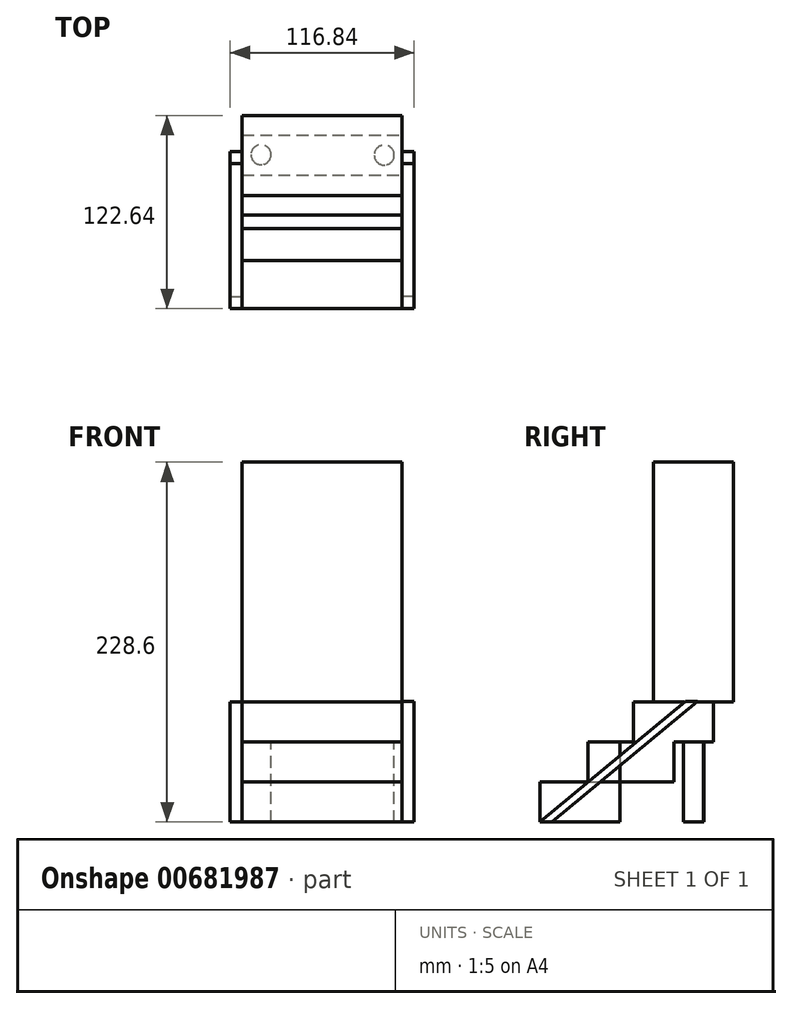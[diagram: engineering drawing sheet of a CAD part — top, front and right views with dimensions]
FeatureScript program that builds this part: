
annotation { "Feature Type Name" : "Feature", "Feature Type Description" : "" }
export const myFeature = defineFeature(function(context is Context, id is Id, definition is map)
    precondition{}
    {
        {
            var Q0;
            Q0=qCreatedBy(makeId("Top.planeOp"),FACE);
            var sketch = newSketch(context, id + "F0", { "sketchPlane" : qUnion([Q0])});
            skLineSegment(sketch, "E0.bottom", {"start": v(-36.45, 27.56) * mm, "end": v(65.15, 27.56) * mm});
            skLineSegment(sketch, "E0.top", {"start": v(-36.45, -23.24) * mm, "end": v(65.15, -23.24) * mm});
            skLineSegment(sketch, "E0.left", {"start": v(-36.45, 27.56) * mm, "end": v(-36.45, -23.24) * mm});
            skLineSegment(sketch, "E0.right", {"start": v(65.15, 27.56) * mm, "end": v(65.15, -23.24) * mm});
            skSolve(sketch);
        }
        {
            var Q0;
            Q0=makeQuery(id+"F0.imprint","IMPRINT",FACE,{"disambiguationData":[TD([[makeQuery(id+"F0.imprint","IMPRINT",EDGE,{"derivedFrom":sQuery(id+"F0.wireOp",EDGE,"E0.bottom")}),-1.0]])]});
            extrude(context, id + "F1", {"entities" : qUnion([Q0]), "depth" : 25.4 * mm, "offsetDistance" : 25.4 * mm});
        }
        {
            var Q0;
            Q0=makeQuery(id+"F1.opExtrude","CAP_FACE",FACE,{"disambiguationData":[OSD([sQuery(id+"F0.wireOp",EDGE,"E0.bottom"),sQuery(id+"F0.wireOp",EDGE,"E0.top"),sQuery(id+"F0.wireOp",EDGE,"E0.left"),sQuery(id+"F0.wireOp",EDGE,"E0.right")])],"isStart":false});
            var sketch = newSketch(context, id + "F2", { "sketchPlane" : qUnion([Q0])});
            skLineSegment(sketch, "E1.bottom", {"start": v(-36.45, 10.8) * mm, "end": v(65.15, 10.8) * mm});
            skLineSegment(sketch, "E1.top", {"start": v(-36.45, 61.6) * mm, "end": v(65.15, 61.6) * mm});
            skLineSegment(sketch, "E1.left", {"start": v(-36.45, 10.8) * mm, "end": v(-36.45, 61.6) * mm});
            skLineSegment(sketch, "E1.right", {"start": v(65.15, 10.8) * mm, "end": v(65.15, 61.6) * mm});
            skSolve(sketch);
        }
        {
            var Q0;
            {var subQ3=sQuery(id+"F2.wireOp",EDGE,"E1.top");Q0=makeQuery(id+"F2.imprint","IMPRINT",FACE,{"disambiguationData":[TD([[makeQuery(id+"F2.imprint","IMPRINT",EDGE,{"derivedFrom":subQ3}),-1.0]])]});}
            extrude(context, id + "F3", {"entities" : qUnion([Q0]), "depth" : 25.4 * mm, "offsetDistance" : 25.4 * mm});
        }
        {
            var Q0;
            Q0=makeQuery(id+"F3.opExtrude","SWEPT_FACE",FACE,{"disambiguationData":[OSD([sQuery(id+"F0.wireOp",EDGE,"E0.bottom")])]});
            extrude(context, id + "F4", {"entities" : qUnion([Q0]), "depth" : 20.32 * mm, "offsetDistance" : 25.4 * mm});
        }
        {
            var Q0;
            Q0=makeQuery(id+"F3.opExtrude","CAP_FACE",FACE,{"disambiguationData":[OSD([sQuery(id+"F0.wireOp",EDGE,"E0.bottom"),sQuery(id+"F0.wireOp",EDGE,"E0.right"),sQuery(id+"F2.wireOp",EDGE,"E1.bottom"),sQuery(id+"F2.wireOp",EDGE,"E1.top"),sQuery(id+"F2.wireOp",EDGE,"E1.left"),sQuery(id+"F2.wireOp",EDGE,"E1.right")])],"isStart":false});
            var sketch = newSketch(context, id + "F5", { "sketchPlane" : qUnion([Q0])});
            skLineSegment(sketch, "E2.bottom", {"start": v(-36.45, 36.13) * mm, "end": v(65.15, 36.13) * mm});
            skLineSegment(sketch, "E2.top", {"start": v(-36.45, 86.93) * mm, "end": v(65.15, 86.93) * mm});
            skLineSegment(sketch, "E2.left", {"start": v(-36.45, 36.13) * mm, "end": v(-36.45, 86.93) * mm});
            skLineSegment(sketch, "E2.right", {"start": v(65.15, 36.13) * mm, "end": v(65.15, 86.93) * mm});
            skSolve(sketch);
        }
        {
            var Q0;
            {var subQ0=sQuery(id+"F5.wireOp",EDGE,"E2.top");Q0=makeQuery(id+"F5.imprint","IMPRINT",FACE,{"disambiguationData":[TD([[makeQuery(id+"F5.imprint","IMPRINT",EDGE,{"derivedFrom":subQ0}),-1.0]])]});}
            var Q1;
            {var subQ0=sQuery(id+"F5.wireOp",EDGE,"E2.bottom");Q1=makeQuery(id+"F5.imprint","IMPRINT",FACE,{"disambiguationData":[TD([[makeQuery(id+"F5.imprint","IMPRINT",EDGE,{"derivedFrom":subQ0}),1.0]])]});}
            extrude(context, id + "F6", {"entities" : qUnion([Q0, Q1]), "operationType" : NewBodyOperationType.ADD, "depth" : 25.4 * mm, "offsetDistance" : 25.4 * mm});
        }
        {
            var Q0;
            Q0=makeQuery(id+"F6.opExtrude","CAP_FACE",FACE,{"disambiguationData":[OSD([sQuery(id+"F5.wireOp",EDGE,"E2.bottom"),sQuery(id+"F5.wireOp",EDGE,"E2.top"),sQuery(id+"F5.wireOp",EDGE,"E2.left"),sQuery(id+"F5.wireOp",EDGE,"E2.right")])],"isStart":true});
            var sketch = newSketch(context, id + "F7", { "sketchPlane" : qUnion([Q0])});
            skCircle(sketch, "E3", {"center": v(-24.5, -74.53) * mm, "radius": 6.35 * mm});
            skCircle(sketch, "E4", {"center": v(53.76, -74.26) * mm, "radius": 6.35 * mm});
            skPoint(sketch, "E4.centerSnap0", {"position": v(-36.45, -74.26) * mm});
            skSolve(sketch);
        }
        {
            var Q0;
            Q0=makeQuery(id+"F7.imprint","IMPRINT",FACE,{"disambiguationData":[TD([[makeQuery(id+"F7.imprint","IMPRINT",EDGE,{"derivedFrom":sQuery(id+"F7.wireOp",EDGE,"E3")}),1.0]])]});
            var Q1;
            Q1=makeQuery(id+"F7.imprint","IMPRINT",FACE,{"disambiguationData":[TD([[makeQuery(id+"F7.imprint","IMPRINT",EDGE,{"derivedFrom":sQuery(id+"F7.wireOp",EDGE,"E4")}),1.0]])]});
            extrude(context, id + "F8", {"entities" : qUnion([Q0, Q1]), "operationType" : NewBodyOperationType.ADD, "depth" : 50.8 * mm, "offsetDistance" : 25.4 * mm});
        }
        {
            var Q0;
            Q0=makeQuery(id+"F1.opExtrude","SWEPT_FACE",FACE,{"disambiguationData":[OSD([sQuery(id+"F0.wireOp",EDGE,"E0.right")])]});
            var sketch = newSketch(context, id + "F9", { "sketchPlane" : qUnion([Q0])});
            skLineSegment(sketch, "E5", {"start": v(-23.24, 0) * mm, "end": v(69.02, 76.69) * mm});
            skLineSegment(sketch, "E6", {"start": v(69.02, 76.69) * mm, "end": v(76.64, 76.69) * mm});
            skLineSegment(sketch, "E7", {"start": v(76.64, 76.69) * mm, "end": v(-15.62, 0) * mm});
            skLineSegment(sketch, "E8", {"start": v(-15.62, 0) * mm, "end": v(-23.24, 0) * mm});
            skSolve(sketch);
        }
        {
            var Q0;
            {var subQ0=sQuery(id+"F9.wireOp",EDGE,"E8");Q0=makeQuery(id+"F9.imprint","IMPRINT",FACE,{"disambiguationData":[TD([[makeQuery(id+"F9.imprint","IMPRINT",EDGE,{"derivedFrom":subQ0}),-1.0]])]});}
            var Q1;
            {var subQ0=sQuery(id+"F9.wireOp",EDGE,"E6");Q1=makeQuery(id+"F9.imprint","IMPRINT",FACE,{"disambiguationData":[TD([[makeQuery(id+"F9.imprint","IMPRINT",EDGE,{"derivedFrom":subQ0}),-1.0]])]});}
            extrude(context, id + "F10", {"entities" : qUnion([Q0, Q1]), "depth" : 7.62 * mm, "offsetDistance" : 25.4 * mm});
        }
        {
            var Q0;
            Q0=makeQuery(id+"F1.opExtrude","SWEPT_FACE",FACE,{"disambiguationData":[OSD([sQuery(id+"F0.wireOp",EDGE,"E0.left")])]});
            var sketch = newSketch(context, id + "F11", { "sketchPlane" : qUnion([Q0])});
            skLineSegment(sketch, "E9", {"start": v(23.24, 0) * mm, "end": v(-68.86, 76.32) * mm});
            skLineSegment(sketch, "E10", {"start": v(-68.86, 76.32) * mm, "end": v(-76.48, 76.32) * mm});
            skLineSegment(sketch, "E11", {"start": v(-76.48, 76.32) * mm, "end": v(15.62, 0) * mm});
            skLineSegment(sketch, "E12", {"start": v(15.62, 0) * mm, "end": v(23.24, 0) * mm});
            skSolve(sketch);
        }
        {
            var Q0;
            {var subQ0=sQuery(id+"F11.wireOp",EDGE,"E10");Q0=makeQuery(id+"F11.imprint","IMPRINT",FACE,{"disambiguationData":[TD([[makeQuery(id+"F11.imprint","IMPRINT",EDGE,{"derivedFrom":subQ0}),1.0]])]});}
            var Q1;
            {var subQ0=sQuery(id+"F11.wireOp",EDGE,"E12");Q1=makeQuery(id+"F11.imprint","IMPRINT",FACE,{"disambiguationData":[TD([[makeQuery(id+"F11.imprint","IMPRINT",EDGE,{"derivedFrom":subQ0}),1.0]])]});}
            extrude(context, id + "F12", {"entities" : qUnion([Q0, Q1]), "depth" : 7.62 * mm, "offsetDistance" : 25.4 * mm});
        }
        {
            var Q0;
            Q0=makeQuery(id+"F6.opExtrude","CAP_FACE",FACE,{"disambiguationData":[OSD([sQuery(id+"F5.wireOp",EDGE,"E2.bottom"),sQuery(id+"F5.wireOp",EDGE,"E2.top"),sQuery(id+"F5.wireOp",EDGE,"E2.left"),sQuery(id+"F5.wireOp",EDGE,"E2.right")])],"isStart":false});
            var sketch = newSketch(context, id + "F13", { "sketchPlane" : qUnion([Q0])});
            skLineSegment(sketch, "E13.bottom", {"start": v(-36.45, 48.6) * mm, "end": v(65.15, 48.6) * mm});
            skLineSegment(sketch, "E13.top", {"start": v(-36.45, 99.4) * mm, "end": v(65.15, 99.4) * mm});
            skLineSegment(sketch, "E13.left", {"start": v(-36.45, 48.6) * mm, "end": v(-36.45, 99.4) * mm});
            skLineSegment(sketch, "E13.right", {"start": v(65.15, 48.6) * mm, "end": v(65.15, 99.4) * mm});
            skSolve(sketch);
        }
        {
            var Q0;
            {var subQ0=sQuery(id+"F13.wireOp",EDGE,"E13.top");Q0=makeQuery(id+"F13.imprint","IMPRINT",FACE,{"disambiguationData":[TD([[makeQuery(id+"F13.imprint","IMPRINT",EDGE,{"derivedFrom":subQ0}),-1.0]])]});}
            var Q1;
            {var subQ0=sQuery(id+"F13.wireOp",EDGE,"E13.bottom");Q1=makeQuery(id+"F13.imprint","IMPRINT",FACE,{"disambiguationData":[TD([[makeQuery(id+"F13.imprint","IMPRINT",EDGE,{"derivedFrom":subQ0}),1.0]])]});}
            extrude(context, id + "F14", {"entities" : qUnion([Q0, Q1]), "depth" : 152.4 * mm, "offsetDistance" : 25.4 * mm});
        }
    });
